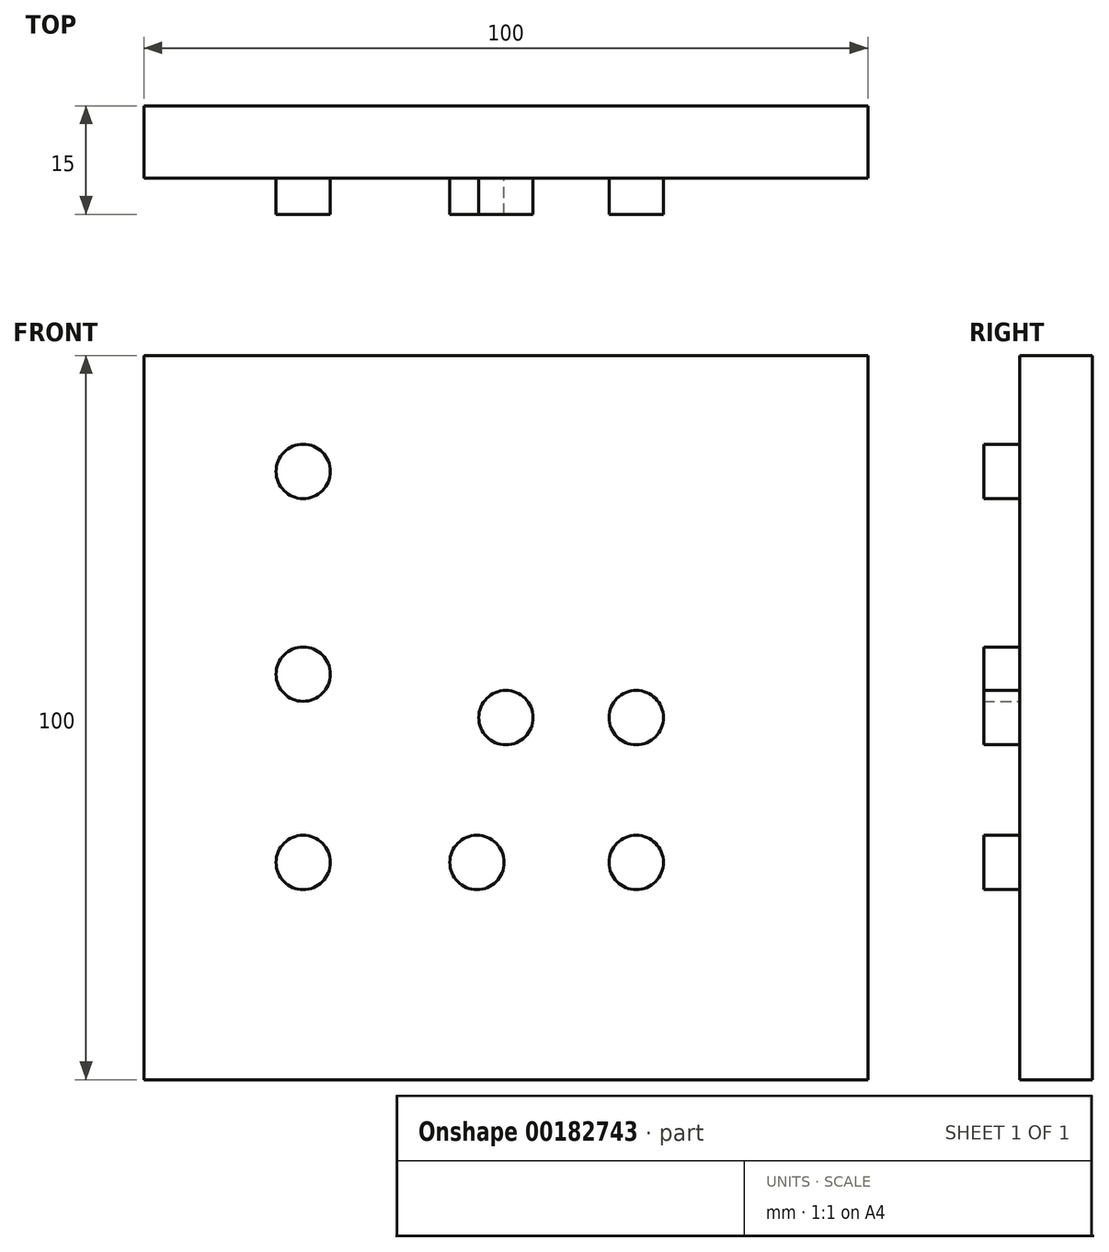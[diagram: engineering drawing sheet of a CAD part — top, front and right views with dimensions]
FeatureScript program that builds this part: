
annotation { "Feature Type Name" : "Feature", "Feature Type Description" : "" }
export const myFeature = defineFeature(function(context is Context, id is Id, definition is map)
    precondition{}
    {
        {
            var Q0;
            Q0=qCreatedBy(makeId("Front.planeOp"),FACE);
            var sketch = newSketch(context, id + "F0", { "sketchPlane" : qUnion([Q0])});
            skLineSegment(sketch, "E0.bottom", {"start": v(-50, 50) * mm, "end": v(50, 50) * mm});
            skLineSegment(sketch, "E0.top", {"start": v(-50, -50) * mm, "end": v(50, -50) * mm});
            skLineSegment(sketch, "E0.left", {"start": v(-50, 50) * mm, "end": v(-50, -50) * mm});
            skLineSegment(sketch, "E0.right", {"start": v(50, 50) * mm, "end": v(50, -50) * mm});
            skPoint(sketch, "E0.middle", {"position": v(0, 0) * mm});
            skSolve(sketch);
        }
        {
            var Q0;
            Q0 = qSketchRegion(id + "F0", true);
            extrude(context, id + "F1", {"entities" : qUnion([Q0]), "depth" : 10 * mm});
        }
        {
            var Q0;
            Q0=makeQuery(id+"F1.opExtrude","CAP_FACE",FACE,{"disambiguationData":[OSD([sQuery(id+"F0.wireOp",EDGE,"E0.bottom"),sQuery(id+"F0.wireOp",EDGE,"E0.top"),sQuery(id+"F0.wireOp",EDGE,"E0.left"),sQuery(id+"F0.wireOp",EDGE,"E0.right")])],"isStart":false});
            var sketch = newSketch(context, id + "F2", { "sketchPlane" : qUnion([Q0])});
            skCircle(sketch, "E1", {"center": v(0, 0) * mm, "radius": 3.75 * mm});
            skSolve(sketch);
        }
        {
            var Q0;
            Q0=makeQuery(id+"F2.imprint","IMPRINT",FACE,{"disambiguationData":[TD([[makeQuery(id+"F2.imprint","IMPRINT",EDGE,{"derivedFrom":sQuery(id+"F2.wireOp",EDGE,"E1")}),1.0]])]});
            var Q1;
            Q1=sQuery(id+"F2.wireOp",EDGE,"E1");
            extrude(context, id + "F3", {"entities" : qUnion([Q0]), "operationType" : NewBodyOperationType.ADD, "surfaceEntities" : qUnion([Q1]), "depth" : 5 * mm});
        }
        {
            var Q0;
            Q0=makeQuery(id+"F1.opExtrude","CAP_FACE",FACE,{"disambiguationData":[OSD([sQuery(id+"F0.wireOp",EDGE,"E0.bottom"),sQuery(id+"F0.wireOp",EDGE,"E0.top"),sQuery(id+"F0.wireOp",EDGE,"E0.left"),sQuery(id+"F0.wireOp",EDGE,"E0.right")])],"isStart":false});
            var sketch = newSketch(context, id + "F4", { "sketchPlane" : qUnion([Q0])});
            skCircle(sketch, "E2", {"center": v(18, 0) * mm, "radius": 3.75 * mm});
            skSolve(sketch);
        }
        {
            var Q0;
            Q0=makeQuery(id+"F4.imprint","IMPRINT",FACE,{"disambiguationData":[TD([[makeQuery(id+"F4.imprint","IMPRINT",EDGE,{"derivedFrom":sQuery(id+"F4.wireOp",EDGE,"E2")}),1.0]])]});
            extrude(context, id + "F5", {"entities" : qUnion([Q0]), "operationType" : NewBodyOperationType.ADD, "depth" : 5 * mm});
        }
        {
            var Q0;
            Q0=makeQuery(id+"F1.opExtrude","CAP_FACE",FACE,{"disambiguationData":[OSD([sQuery(id+"F0.wireOp",EDGE,"E0.bottom"),sQuery(id+"F0.wireOp",EDGE,"E0.top"),sQuery(id+"F0.wireOp",EDGE,"E0.left"),sQuery(id+"F0.wireOp",EDGE,"E0.right")])],"isStart":false});
            var sketch = newSketch(context, id + "F6", { "sketchPlane" : qUnion([Q0])});
            skCircle(sketch, "E3", {"center": v(18, -20) * mm, "radius": 3.75 * mm});
            skSolve(sketch);
        }
        {
            var Q0;
            Q0=makeQuery(id+"F1.opExtrude","CAP_FACE",FACE,{"disambiguationData":[OSD([sQuery(id+"F0.wireOp",EDGE,"E0.bottom"),sQuery(id+"F0.wireOp",EDGE,"E0.top"),sQuery(id+"F0.wireOp",EDGE,"E0.left"),sQuery(id+"F0.wireOp",EDGE,"E0.right")])],"isStart":false});
            var sketch = newSketch(context, id + "F7", { "sketchPlane" : qUnion([Q0])});
            skCircle(sketch, "E4", {"center": v(-4, -20) * mm, "radius": 3.75 * mm});
            skCircle(sketch, "E5.0", {"center": v(18, -20) * mm, "radius": 3.75 * mm});
            skSolve(sketch);
        }
        {
            var Q0;
            Q0=makeQuery(id+"F7.imprint","IMPRINT",FACE,{"disambiguationData":[TD([[makeQuery(id+"F7.imprint","IMPRINT",EDGE,{"derivedFrom":sQuery(id+"F7.wireOp",EDGE,"E4")}),1.0]])]});
            var Q1;
            Q1=sQuery(id+"F7.wireOp",EDGE,"E4");
            extrude(context, id + "F8", {"entities" : qUnion([Q0]), "operationType" : NewBodyOperationType.ADD, "surfaceEntities" : qUnion([Q1]), "depth" : 5 * mm});
        }
        {
            var Q0;
            Q0=makeQuery(id+"F1.opExtrude","CAP_FACE",FACE,{"disambiguationData":[OSD([sQuery(id+"F0.wireOp",EDGE,"E0.bottom"),sQuery(id+"F0.wireOp",EDGE,"E0.top"),sQuery(id+"F0.wireOp",EDGE,"E0.left"),sQuery(id+"F0.wireOp",EDGE,"E0.right")])],"isStart":false});
            var sketch = newSketch(context, id + "F9", { "sketchPlane" : qUnion([Q0])});
            skCircle(sketch, "E6", {"center": v(-28, -20) * mm, "radius": 3.75 * mm});
            skCircle(sketch, "E7.0", {"center": v(-4, -20) * mm, "radius": 3.75 * mm});
            skSolve(sketch);
        }
        {
            var Q0;
            Q0=makeQuery(id+"F9.imprint","IMPRINT",FACE,{"disambiguationData":[TD([[makeQuery(id+"F9.imprint","IMPRINT",EDGE,{"derivedFrom":sQuery(id+"F9.wireOp",EDGE,"E6")}),1.0]])]});
            extrude(context, id + "F10", {"entities" : qUnion([Q0]), "operationType" : NewBodyOperationType.ADD, "depth" : 5 * mm});
        }
        {
            var Q0;
            Q0=makeQuery(id+"F1.opExtrude","CAP_FACE",FACE,{"disambiguationData":[OSD([sQuery(id+"F0.wireOp",EDGE,"E0.bottom"),sQuery(id+"F0.wireOp",EDGE,"E0.top"),sQuery(id+"F0.wireOp",EDGE,"E0.left"),sQuery(id+"F0.wireOp",EDGE,"E0.right")])],"isStart":false});
            var sketch = newSketch(context, id + "F11", { "sketchPlane" : qUnion([Q0])});
            skCircle(sketch, "E8.0", {"center": v(-28, -20) * mm, "radius": 3.75 * mm});
            skCircle(sketch, "E9", {"center": v(-28, 6) * mm, "radius": 3.75 * mm});
            skSolve(sketch);
        }
        {
            var Q0;
            Q0=makeQuery(id+"F11.imprint","IMPRINT",FACE,{"disambiguationData":[TD([[makeQuery(id+"F11.imprint","IMPRINT",EDGE,{"derivedFrom":sQuery(id+"F11.wireOp",EDGE,"E9")}),1.0]])]});
            extrude(context, id + "F12", {"entities" : qUnion([Q0]), "operationType" : NewBodyOperationType.ADD, "depth" : 5 * mm});
        }
        {
            var Q0;
            Q0=makeQuery(id+"F1.opExtrude","CAP_FACE",FACE,{"disambiguationData":[OSD([sQuery(id+"F0.wireOp",EDGE,"E0.bottom"),sQuery(id+"F0.wireOp",EDGE,"E0.top"),sQuery(id+"F0.wireOp",EDGE,"E0.left"),sQuery(id+"F0.wireOp",EDGE,"E0.right")])],"isStart":false});
            var sketch = newSketch(context, id + "F13", { "sketchPlane" : qUnion([Q0])});
            skCircle(sketch, "E10.0", {"center": v(-28, 6) * mm, "radius": 3.75 * mm});
            skCircle(sketch, "E11", {"center": v(-28, 34) * mm, "radius": 3.75 * mm});
            skSolve(sketch);
        }
        {
            var Q0;
            Q0=makeQuery(id+"F13.imprint","IMPRINT",FACE,{"disambiguationData":[TD([[makeQuery(id+"F13.imprint","IMPRINT",EDGE,{"derivedFrom":sQuery(id+"F13.wireOp",EDGE,"E11")}),1.0]])]});
            extrude(context, id + "F14", {"entities" : qUnion([Q0]), "operationType" : NewBodyOperationType.ADD, "depth" : 5 * mm});
        }
        {
            var Q0;
            Q0=makeQuery(id+"F6.imprint","IMPRINT",FACE,{"disambiguationData":[TD([[makeQuery(id+"F6.imprint","IMPRINT",EDGE,{"derivedFrom":sQuery(id+"F6.wireOp",EDGE,"E3")}),1.0]])]});
            extrude(context, id + "F15", {"entities" : qUnion([Q0]), "operationType" : NewBodyOperationType.ADD, "depth" : 5 * mm});
        }
    });
